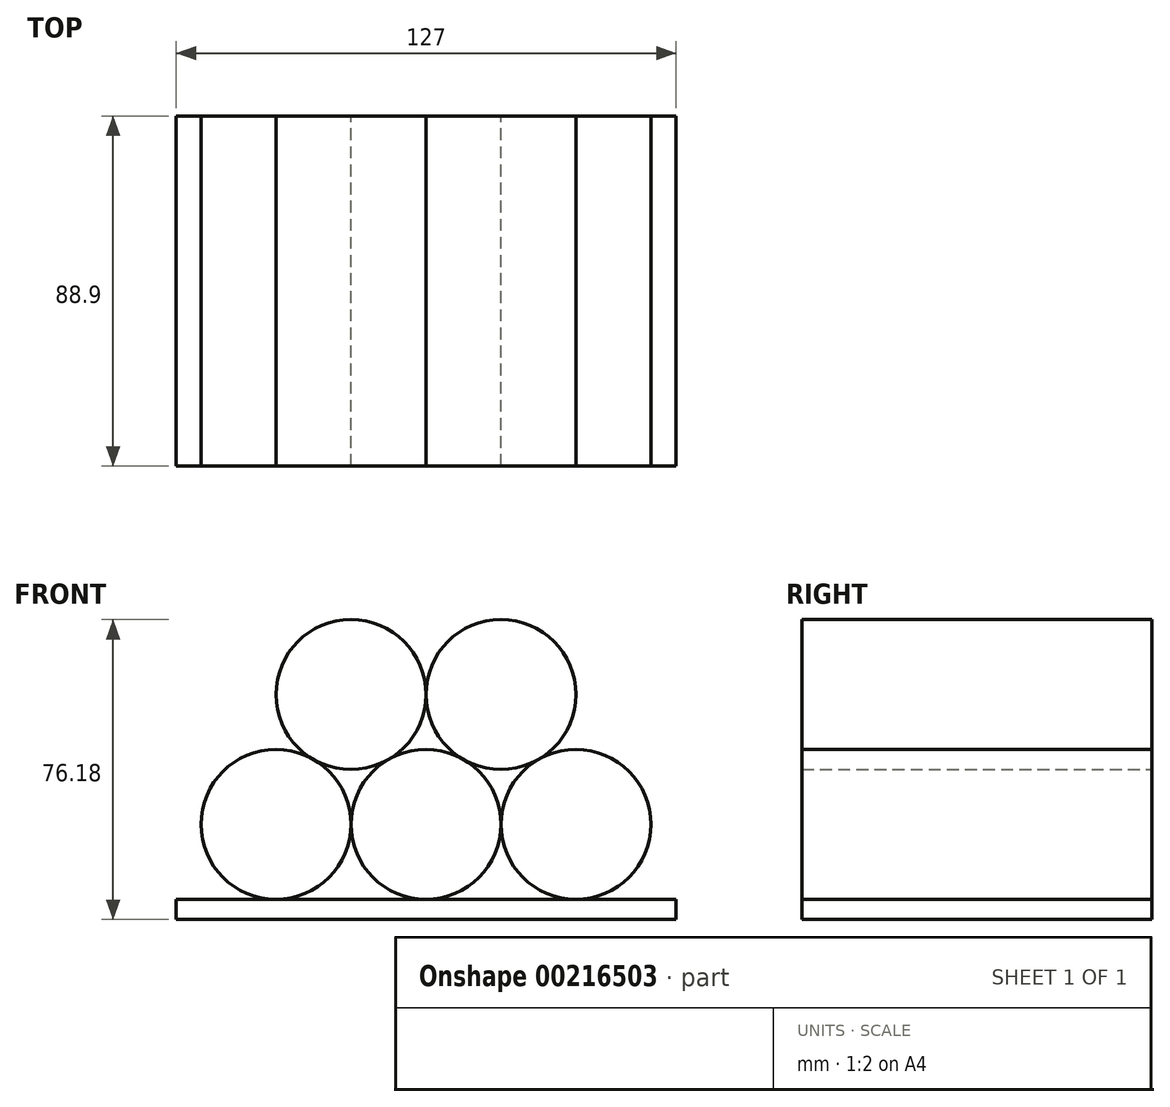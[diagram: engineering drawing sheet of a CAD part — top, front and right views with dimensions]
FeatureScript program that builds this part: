
annotation { "Feature Type Name" : "Feature", "Feature Type Description" : "" }
export const myFeature = defineFeature(function(context is Context, id is Id, definition is map)
    precondition{}
    {
        {
            var Q0;
            Q0=qCreatedBy(makeId("Front.planeOp"),FACE);
            var sketch = newSketch(context, id + "F0", { "sketchPlane" : qUnion([Q0])});
            skCircle(sketch, "E0", {"center": v(-19.11, 6.18) * mm, "radius": 19.05 * mm});
            skCircle(sketch, "E1", {"center": v(18.99, 6.18) * mm, "radius": 19.05 * mm});
            skCircle(sketch, "E2", {"center": v(-38.16, -26.82) * mm, "radius": 19.05 * mm});
            skCircle(sketch, "E3", {"center": v(-0.06, -26.82) * mm, "radius": 19.05 * mm});
            skCircle(sketch, "E4", {"center": v(38.04, -26.82) * mm, "radius": 19.05 * mm});
            skLineSegment(sketch, "E5", {"start": v(38.04, -26.82) * mm, "end": v(-48.43, -26.82) * mm, "construction": true});
            skLineSegment(sketch, "E6.bottom", {"start": v(-63.5, -45.87) * mm, "end": v(63.5, -45.87) * mm});
            skLineSegment(sketch, "E6.top", {"start": v(-63.5, -50.95) * mm, "end": v(63.5, -50.95) * mm});
            skLineSegment(sketch, "E6.left", {"start": v(-63.5, -45.87) * mm, "end": v(-63.5, -50.95) * mm});
            skLineSegment(sketch, "E6.right", {"start": v(63.5, -45.87) * mm, "end": v(63.5, -50.95) * mm});
            skSolve(sketch);
        }
        {
            var Q0;
            {var subQ0=sQuery(id+"F0.wireOp",EDGE,"E0");var subQ1=makeQuery(id+"F0.imprint","INTERSECT",VERTEX,{"derivedFrom":[subQ0,sQuery(id+"F0.wireOp",EDGE,"E2")]});Q0=makeQuery(id+"F0.imprint","IMPRINT",FACE,{"disambiguationData":[TD([[makeQuery(id+"F0.imprint","IMPRINT",EDGE,{"disambiguationData":[TD([[subQ1,1.0]])],"derivedFrom":subQ0}),1.0]])]});}
            var Q1;
            {var subQ0=sQuery(id+"F0.wireOp",EDGE,"E1");var subQ1=makeQuery(id+"F0.imprint","INTERSECT",VERTEX,{"derivedFrom":[sQuery(id+"F0.wireOp",EDGE,"E0"),subQ0]});Q1=makeQuery(id+"F0.imprint","IMPRINT",FACE,{"disambiguationData":[TD([[makeQuery(id+"F0.imprint","IMPRINT",EDGE,{"disambiguationData":[TD([[subQ1,-1.0]])],"derivedFrom":subQ0}),1.0]])]});}
            var Q2;
            {var subQ0=sQuery(id+"F0.wireOp",EDGE,"E3");var subQ4=makeQuery(id+"F0.imprint","INTERSECT",VERTEX,{"derivedFrom":[sQuery(id+"F0.wireOp",EDGE,"E1"),subQ0]});Q2=makeQuery(id+"F0.imprint","IMPRINT",FACE,{"disambiguationData":[TD([[makeQuery(id+"F0.imprint","IMPRINT",EDGE,{"disambiguationData":[TD([[subQ4,1.0]])],"derivedFrom":subQ0}),1.0]])]});}
            var Q3;
            {var subQ0=sQuery(id+"F0.wireOp",EDGE,"E4");var subQ1=makeQuery(id+"F0.imprint","INTERSECT",VERTEX,{"derivedFrom":[sQuery(id+"F0.wireOp",EDGE,"E1"),subQ0]});Q3=makeQuery(id+"F0.imprint","IMPRINT",FACE,{"disambiguationData":[TD([[makeQuery(id+"F0.imprint","IMPRINT",EDGE,{"disambiguationData":[TD([[subQ1,-1.0]])],"derivedFrom":subQ0}),1.0]])]});}
            var Q4;
            {var subQ0=sQuery(id+"F0.wireOp",EDGE,"E2");var subQ1=makeQuery(id+"F0.imprint","INTERSECT",VERTEX,{"derivedFrom":[sQuery(id+"F0.wireOp",EDGE,"E0"),subQ0]});Q4=makeQuery(id+"F0.imprint","IMPRINT",FACE,{"disambiguationData":[TD([[makeQuery(id+"F0.imprint","IMPRINT",EDGE,{"disambiguationData":[TD([[subQ1,1.0]])],"derivedFrom":subQ0}),1.0]])]});}
            var Q5;
            Q5=makeQuery(id+"F0.imprint","IMPRINT",FACE,{"disambiguationData":[TD([[makeQuery(id+"F0.imprint","IMPRINT",EDGE,{"derivedFrom":sQuery(id+"F0.wireOp",EDGE,"E6.top")}),1.0]])]});
            var Q6;
            Q6=sQuery(id+"F0.wireOp",EDGE,"E0");
            var Q7;
            Q7=sQuery(id+"F0.wireOp",EDGE,"E1");
            var Q8;
            Q8=sQuery(id+"F0.wireOp",EDGE,"E2");
            var Q9;
            Q9=sQuery(id+"F0.wireOp",EDGE,"E3");
            var Q10;
            Q10=sQuery(id+"F0.wireOp",EDGE,"E4");
            var Q11;
            Q11=sQuery(id+"F0.wireOp",EDGE,"E6.bottom");
            var Q12;
            Q12=sQuery(id+"F0.wireOp",EDGE,"E6.top");
            var Q13;
            Q13=sQuery(id+"F0.wireOp",EDGE,"E6.left");
            var Q14;
            Q14=sQuery(id+"F0.wireOp",EDGE,"E6.right");
            extrude(context, id + "F1", {"entities" : qUnion([Q0, Q1, Q2, Q3, Q4, Q5]), "surfaceEntities" : qUnion([Q6, Q7, Q8, Q9, Q10, Q11, Q12, Q13, Q14]), "depth" : 88.9 * mm});
        }
    });
